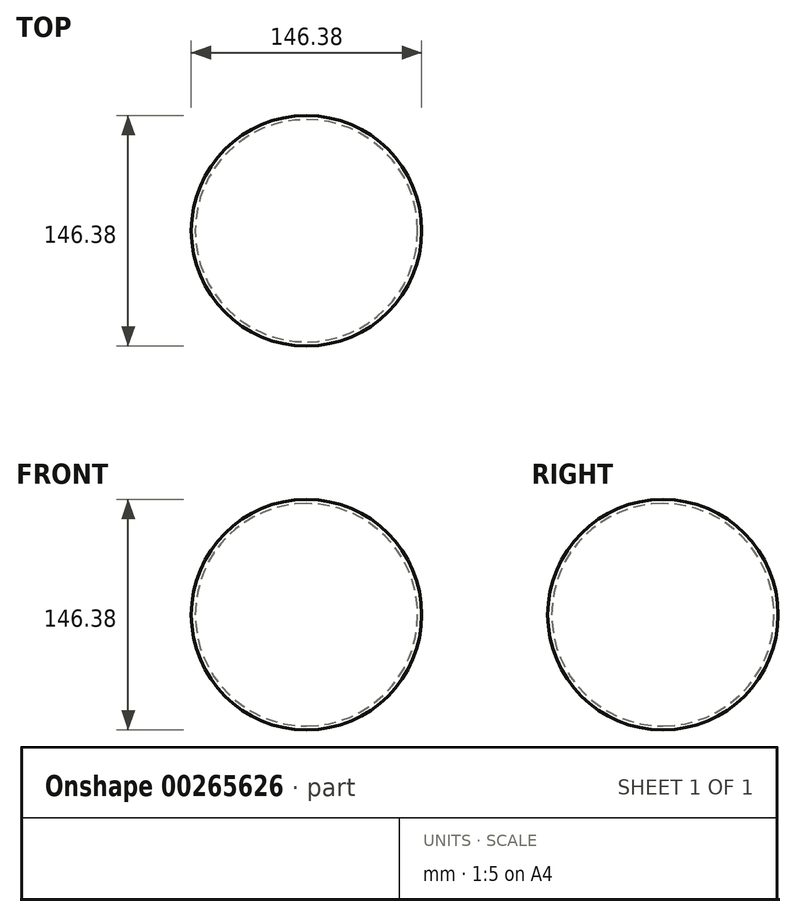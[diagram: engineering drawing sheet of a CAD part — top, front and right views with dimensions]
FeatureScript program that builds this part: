
annotation { "Feature Type Name" : "Feature", "Feature Type Description" : "" }
export const myFeature = defineFeature(function(context is Context, id is Id, definition is map)
    precondition{}
    {
        {
            var Q0;
            Q0=qCreatedBy(makeId("Front.planeOp"),FACE);
            var sketch = newSketch(context, id + "F0", { "sketchPlane" : qUnion([Q0])});
            skCircle(sketch, "E0", {"center": v(0, 0) * mm, "radius": 73.19 * mm});
            skLineSegment(sketch, "E1", {"start": v(0, 73.19) * mm, "end": v(0, -73.19) * mm});
            skPoint(sketch, "E2.orphan", {"position": v(0, 135.55) * mm});
            skSolve(sketch);
        }
        {
            var Q0;
            {var subQ0=sQuery(id+"F0.wireOp",EDGE,"E1");Q0=makeQuery(id+"F0.imprint","IMPRINT",FACE,{"disambiguationData":[TD([[makeQuery(id+"F0.imprint","IMPRINT",EDGE,{"derivedFrom":subQ0}),1.0]])]});}
            var Q1;
            Q1=sQuery(id+"F0.wireOp",EDGE,"E1");
            revolve(context, id + "F1", {"entities" : qUnion([Q0]), "axis" : qUnion([Q1]), "revolveType" : RevolveType.SYMMETRIC, "oppositeDirection" : true, "angle" : 360 * degree});
        }
        {
            var Q0;
            Q0=makeQuery(id+"F1.opRevolve","SWEPT_FACE",FACE,{"disambiguationData":[OSD([sQuery(id+"F0.wireOp",EDGE,"E0")])]});
            var Q1;
            Q1=makeQuery(id+"F1.opRevolve","SWEPT_BODY",BODY,{"disambiguationData":[OSD([sQuery(id+"F0.wireOp",EDGE,"E0"),sQuery(id+"F0.wireOp",EDGE,"E1")])]});
            shell(context, id + "F2", {"isHollow" : true, "entities" : qUnion([Q0]), "parts" : qUnion([Q1]), "thickness" : 2.54 * mm});
        }
    });
